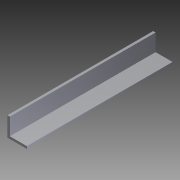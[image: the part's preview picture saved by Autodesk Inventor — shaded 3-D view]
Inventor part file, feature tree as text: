
AUTODESK INVENTOR PART (.ipt)
format: ipt  version: 2012 (Build 160160000, 160)  size: 72,704 bytes
history: native  units: in
note: dims shown in document units (in); Inventor stores cm internally (conversion verified against a paired STEP export)
features: extrude x1, sketch x1
ambient origin geometry x8: Origin, YZ Plane, XZ Plane, XY Plane, X Axis, Y Axis, Z Axis, Center Point
bodies: Solid1 (feature_tree)
feature tree (2):
  extrude  "Extrusion1"  Depth=0.125in
  sketch  "Sketch1"  dims[d0=0.125in d1=0.125in d2=1.0in d3=1.0in d4=7.5in d5=0.0in]
